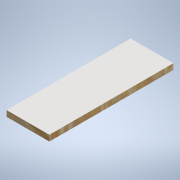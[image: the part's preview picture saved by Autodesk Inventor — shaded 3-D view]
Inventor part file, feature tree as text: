
AUTODESK INVENTOR PART (.ipt)
format: ipt  version: 2021.1 (Build 251245000, 245)  size: 128,512 bytes
history: native  units: in
note: dims shown in document units (in); Inventor stores cm internally (conversion verified against a paired STEP export)
features: other x5, extrude x3, sketch x3, reference x3
ambient origin geometry x8: Origin, YZ Plane, XZ Plane, XY Plane, X Axis, Y Axis, Z Axis, Center Point
bodies: Solid1 (feature_tree)
feature tree (14):
  extrude  "Extrusion1"  Depth=10.6299in TaperAngle=0.0deg
  extrude  "Extrusion2"  [1 undecoded]
  extrude  "Extrusion3"  [1 undecoded]
  sketch  "Sketch1"  dims[d0=10.6299in d1=0.0in d2=0.25in d3=0.0in]
  reference  "Reference1"
  reference  "Reference2"
  reference  "Reference3"
  sketch  "Sketch2"  dims[d4=0.5in d5=0.0in]
  sketch  "Sketch3"
  other  "<userpath>\Documents\Kerbal Kontroller\Design\Final\Inventor\Final.iam"
  other  "Final.iam"
  other  "Sides:1"
  other  "Front:1"
  other  "Bottom:1"
note: 2 required parameter values undecoded (feature->parameter linkage not recoverable at this tier; creation-order binding heuristic only, values carry confidence <= 0.55)
